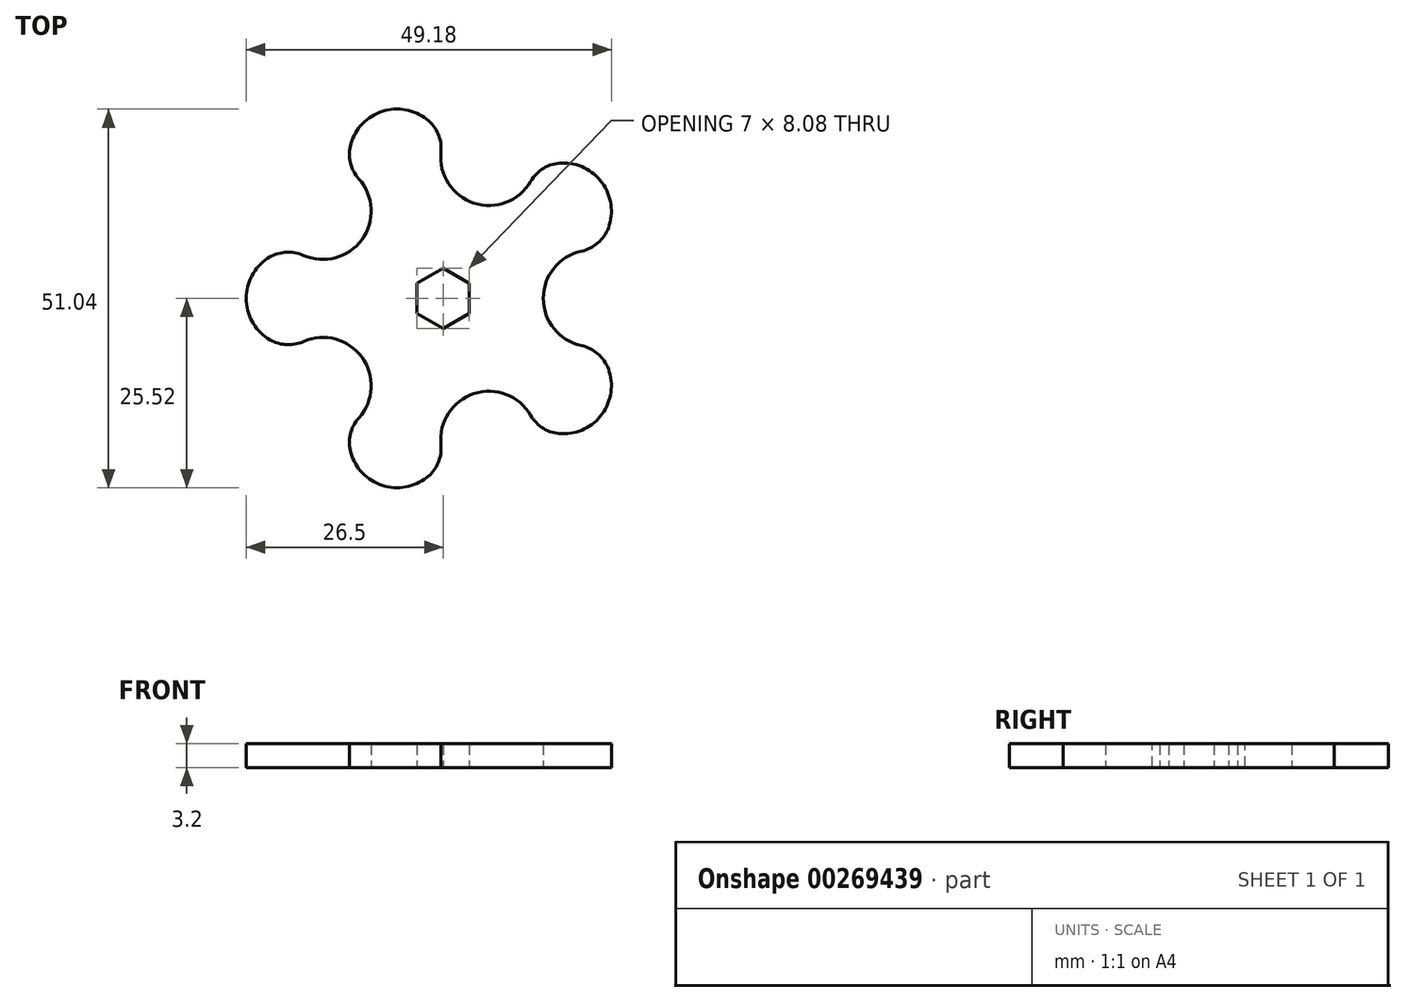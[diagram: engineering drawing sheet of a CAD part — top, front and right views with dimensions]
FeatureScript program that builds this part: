
annotation { "Feature Type Name" : "Feature", "Feature Type Description" : "" }
export const myFeature = defineFeature(function(context is Context, id is Id, definition is map)
    precondition{}
    {
        {
            var Q0;
            Q0=qCreatedBy(makeId("Top.planeOp"),FACE);
            var sketch = newSketch(context, id + "F0", { "sketchPlane" : qUnion([Q0])});
            skCircle(sketch, "E0.cCircle", {"center": v(0, 0) * mm, "radius": 3.5 * mm, "construction": true});
            skLineSegment(sketch, "E0.0", {"start": v(3.5, 2.02) * mm, "end": v(3.5, -2.02) * mm});
            skLineSegment(sketch, "E0.1", {"start": v(3.5, -2.02) * mm, "end": v(0, -4.04) * mm});
            skLineSegment(sketch, "E0.2", {"start": v(0, -4.04) * mm, "end": v(-3.5, -2.02) * mm});
            skLineSegment(sketch, "E0.3", {"start": v(-3.5, -2.02) * mm, "end": v(-3.5, 2.02) * mm});
            skLineSegment(sketch, "E0.4", {"start": v(-3.5, 2.02) * mm, "end": v(0, 4.04) * mm});
            skLineSegment(sketch, "E0.5", {"start": v(0, 4.04) * mm, "end": v(3.5, 2.02) * mm});
            skPoint(sketch, "E0.0.midPoint", {"position": v(3.5, 0) * mm});
            skCircle(sketch, "E1.cCircle", {"center": v(0, 0) * mm, "radius": 20 * mm, "construction": true});
            skLineSegment(sketch, "E1.0", {"start": v(20, 6.5) * mm, "end": v(20, -6.5) * mm, "construction": true});
            skLineSegment(sketch, "E1.1", {"start": v(20, -6.5) * mm, "end": v(12.36, -17.01) * mm, "construction": true});
            skLineSegment(sketch, "E1.2", {"start": v(12.36, -17.01) * mm, "end": v(0, -21.03) * mm, "construction": true});
            skLineSegment(sketch, "E1.3", {"start": v(0, -21.03) * mm, "end": v(-12.36, -17.01) * mm, "construction": true});
            skLineSegment(sketch, "E1.4", {"start": v(-12.36, -17.01) * mm, "end": v(-20, -6.5) * mm, "construction": true});
            skLineSegment(sketch, "E1.5", {"start": v(-20, -6.5) * mm, "end": v(-20, 6.5) * mm, "construction": true});
            skLineSegment(sketch, "E1.6", {"start": v(-20, 6.5) * mm, "end": v(-12.36, 17.01) * mm, "construction": true});
            skLineSegment(sketch, "E1.7", {"start": v(-12.36, 17.01) * mm, "end": v(0, 21.03) * mm, "construction": true});
            skLineSegment(sketch, "E1.8", {"start": v(0, 21.03) * mm, "end": v(12.36, 17.01) * mm, "construction": true});
            skLineSegment(sketch, "E1.9", {"start": v(12.36, 17.01) * mm, "end": v(20, 6.5) * mm, "construction": true});
            skPoint(sketch, "E1.0.midPoint", {"position": v(20, 0) * mm});
            skArc(sketch, "E2", {"start": v(-20, 6.5) * mm, "mid": v(-26.5, 0) * mm, "end": v(-20, -6.5) * mm});
            skArc(sketch, "E3", {"start": v(-20, 6.5) * mm, "mid": v(-10.92, 7.94) * mm, "end": v(-12.36, 17.01) * mm});
            skArc(sketch, "E4", {"start": v(0, 21.03) * mm, "mid": v(-8.19, 25.2) * mm, "end": v(-12.36, 17.01) * mm});
            skArc(sketch, "E5", {"start": v(0, 21.03) * mm, "mid": v(4.17, 12.84) * mm, "end": v(12.36, 17.01) * mm});
            skArc(sketch, "E6", {"start": v(20, 6.5) * mm, "mid": v(21.44, 15.58) * mm, "end": v(12.36, 17.01) * mm});
            skArc(sketch, "E7", {"start": v(20, 6.5) * mm, "mid": v(13.5, 0) * mm, "end": v(20, -6.5) * mm});
            skArc(sketch, "E8", {"start": v(12.36, -17.01) * mm, "mid": v(21.44, -15.58) * mm, "end": v(20, -6.5) * mm});
            skArc(sketch, "E9", {"start": v(12.36, -17.01) * mm, "mid": v(4.17, -12.84) * mm, "end": v(0, -21.03) * mm});
            skArc(sketch, "E10", {"start": v(-12.36, -17.01) * mm, "mid": v(-8.19, -25.2) * mm, "end": v(0, -21.03) * mm});
            skArc(sketch, "E11", {"start": v(-12.36, -17.01) * mm, "mid": v(-10.92, -7.94) * mm, "end": v(-20, -6.5) * mm});
            skSolve(sketch);
        }
        {
            var Q0;
            Q0=makeQuery(id+"F0.imprint","IMPRINT",FACE,{"disambiguationData":[TD([[makeQuery(id+"F0.imprint","IMPRINT",EDGE,{"derivedFrom":sQuery(id+"F0.wireOp",EDGE,"E0.0")}),1.0]])]});
            extrude(context, id + "F1", {"entities" : qUnion([Q0]), "depth" : 3.2 * mm});
        }
        {
            var Q0;
            Q0=makeQuery(id+"F1.opExtrude","SWEPT_EDGE",EDGE,{"disambiguationData":[OSD([sQuery(id+"F0.wireOp",EDGE,"E3"),sQuery(id+"F0.wireOp",EDGE,"E4")])]});
            var Q1;
            Q1=makeQuery(id+"F1.opExtrude","SWEPT_EDGE",EDGE,{"disambiguationData":[OSD([sQuery(id+"F0.wireOp",EDGE,"E2"),sQuery(id+"F0.wireOp",EDGE,"E3")])]});
            var Q2;
            Q2=makeQuery(id+"F1.opExtrude","SWEPT_EDGE",EDGE,{"disambiguationData":[OSD([sQuery(id+"F0.wireOp",EDGE,"E4"),sQuery(id+"F0.wireOp",EDGE,"E5")])]});
            var Q3;
            Q3=makeQuery(id+"F1.opExtrude","SWEPT_EDGE",EDGE,{"disambiguationData":[OSD([sQuery(id+"F0.wireOp",EDGE,"E5"),sQuery(id+"F0.wireOp",EDGE,"E6")])]});
            var Q4;
            Q4=makeQuery(id+"F1.opExtrude","SWEPT_EDGE",EDGE,{"disambiguationData":[OSD([sQuery(id+"F0.wireOp",EDGE,"E6"),sQuery(id+"F0.wireOp",EDGE,"E7")])]});
            var Q5;
            Q5=makeQuery(id+"F1.opExtrude","SWEPT_EDGE",EDGE,{"disambiguationData":[OSD([sQuery(id+"F0.wireOp",EDGE,"E7"),sQuery(id+"F0.wireOp",EDGE,"E8")])]});
            var Q6;
            Q6=makeQuery(id+"F1.opExtrude","SWEPT_EDGE",EDGE,{"disambiguationData":[OSD([sQuery(id+"F0.wireOp",EDGE,"E8"),sQuery(id+"F0.wireOp",EDGE,"E9")])]});
            var Q7;
            Q7=makeQuery(id+"F1.opExtrude","SWEPT_EDGE",EDGE,{"disambiguationData":[OSD([sQuery(id+"F0.wireOp",EDGE,"E9"),sQuery(id+"F0.wireOp",EDGE,"E10")])]});
            var Q8;
            Q8=makeQuery(id+"F1.opExtrude","SWEPT_EDGE",EDGE,{"disambiguationData":[OSD([sQuery(id+"F0.wireOp",EDGE,"E10"),sQuery(id+"F0.wireOp",EDGE,"E11")])]});
            var Q9;
            Q9=makeQuery(id+"F1.opExtrude","SWEPT_EDGE",EDGE,{"disambiguationData":[OSD([sQuery(id+"F0.wireOp",EDGE,"E2"),sQuery(id+"F0.wireOp",EDGE,"E11")])]});
            fillet(context, id + "F2", {"entities" : qUnion([Q0, Q1, Q2, Q3, Q4, Q5, Q6, Q7, Q8, Q9]), "radius" : 5 * mm, "tangentPropagation" : true, "allowEdgeOverflow" : false});
        }
    });
